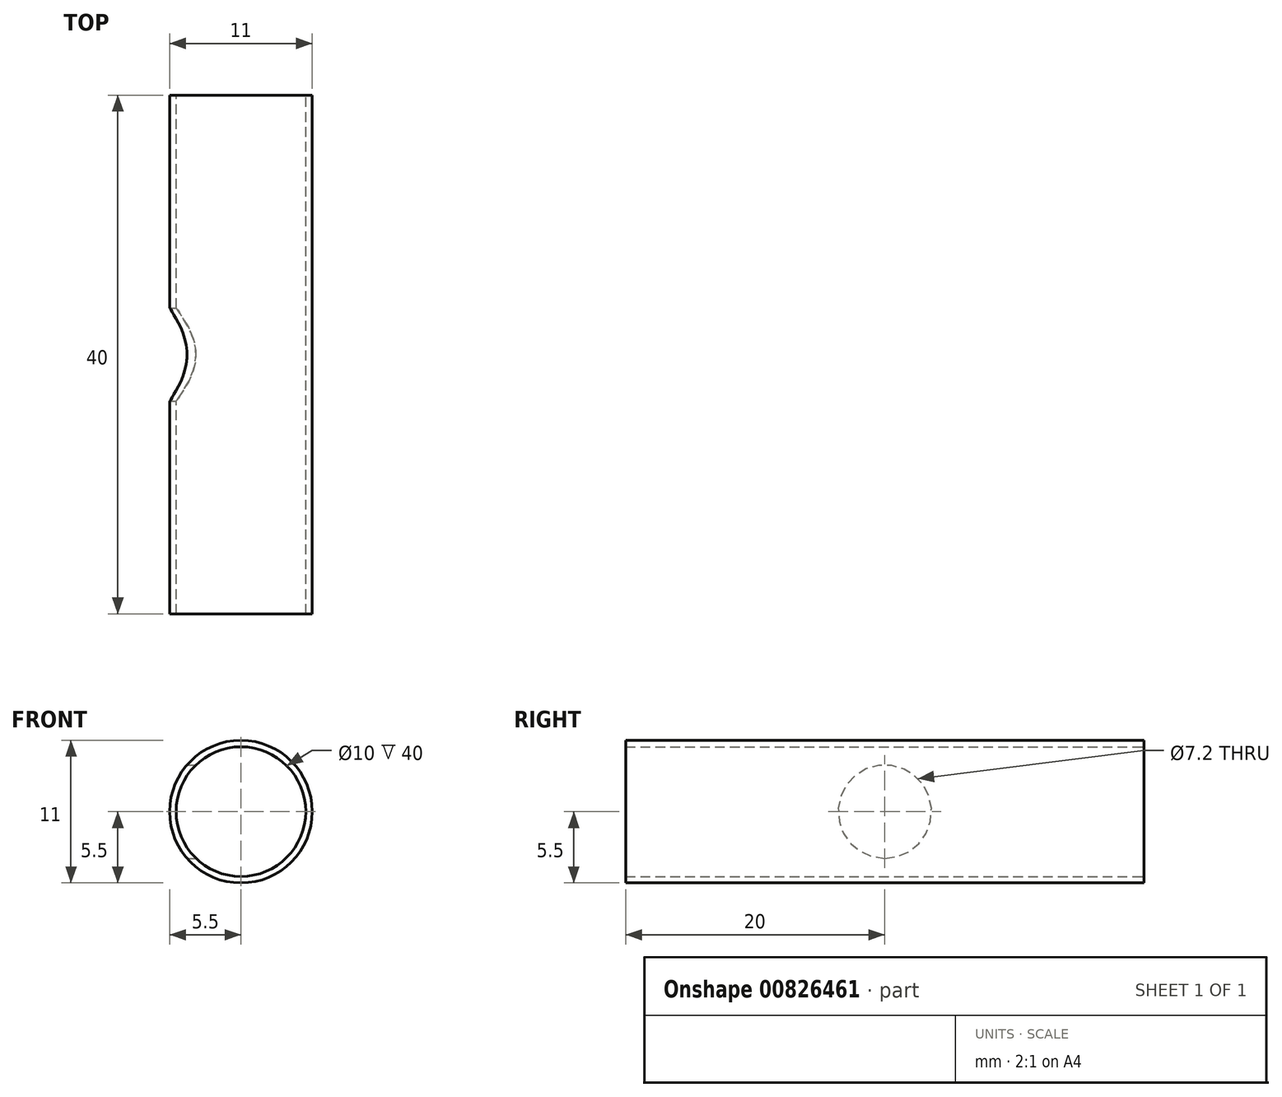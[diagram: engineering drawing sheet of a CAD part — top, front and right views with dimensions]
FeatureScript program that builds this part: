
annotation { "Feature Type Name" : "Feature", "Feature Type Description" : "" }
export const myFeature = defineFeature(function(context is Context, id is Id, definition is map)
    precondition{}
    {
        {
            var Q0;
            Q0=qCreatedBy(makeId("Front.planeOp"),FACE);
            var sketch = newSketch(context, id + "F0", { "sketchPlane" : qUnion([Q0])});
            skCircle(sketch, "E0", {"center": v(0, 0) * mm, "radius": 5 * mm});
            skCircle(sketch, "E1", {"center": v(0, 0) * mm, "radius": 5.5 * mm});
            skSolve(sketch);
        }
        {
            var Q0;
            Q0 = qSketchRegion(id + "F0", true);
            extrude(context, id + "F1", {"entities" : qUnion([Q0]), "endBound" : BoundingType.SYMMETRIC, "depth" : 40 * mm, "offsetDistance" : 25 * mm});
        }
        {
            var Q0;
            Q0=qCreatedBy(makeId("Right.planeOp"),FACE);
            var sketch = newSketch(context, id + "F2", { "sketchPlane" : qUnion([Q0])});
            skCircle(sketch, "E2", {"center": v(0, 0) * mm, "radius": 3.6 * mm});
            skSolve(sketch);
        }
        {
            var Q0;
            Q0 = qSketchRegion(id + "F2", true);
            extrude(context, id + "F3", {"entities" : qUnion([Q0]), "operationType" : NewBodyOperationType.REMOVE, "oppositeDirection" : true, "depth" : 25 * mm, "offsetDistance" : 25 * mm});
        }
    });
